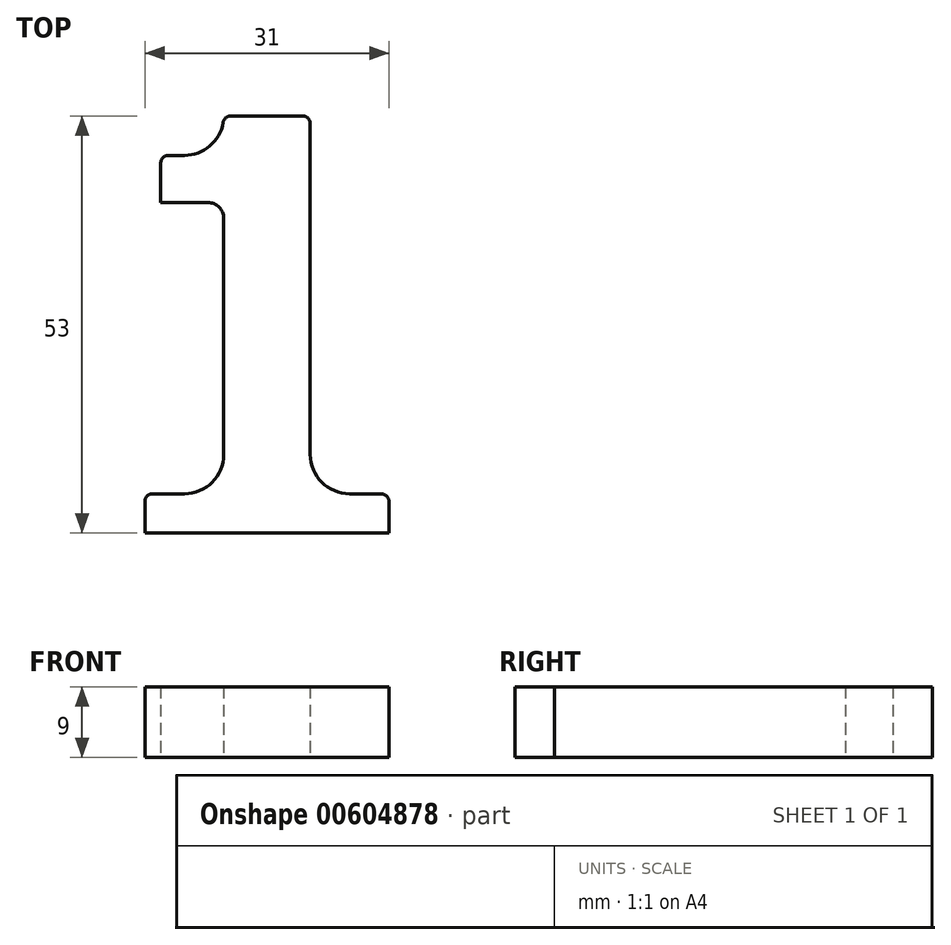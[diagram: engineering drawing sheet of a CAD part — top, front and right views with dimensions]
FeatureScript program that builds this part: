
annotation { "Feature Type Name" : "Feature", "Feature Type Description" : "" }
export const myFeature = defineFeature(function(context is Context, id is Id, definition is map)
    precondition{}
    {
        {
            var Q0;
            Q0=qCreatedBy(makeId("Top.planeOp"),FACE);
            var sketch = newSketch(context, id + "F0", { "sketchPlane" : qUnion([Q0])});
            skLineSegment(sketch, "E0.bottom", {"start": v(5.5, -26.5) * mm, "end": v(-5.5, -26.5) * mm});
            skLineSegment(sketch, "E0.top", {"start": v(5.5, 26.5) * mm, "end": v(-5.5, 26.5) * mm});
            skLineSegment(sketch, "E0.left", {"start": v(5.5, -16.5) * mm, "end": v(5.5, 26.5) * mm});
            skLineSegment(sketch, "E0.right", {"start": v(-5.5, 26.5) * mm, "end": v(-5.5, 26.5) * mm});
            skPoint(sketch, "E0.middle", {"position": v(0, 0) * mm});
            skLineSegment(sketch, "E1.bottom", {"start": v(-5.5, -26.5) * mm, "end": v(-15.5, -26.5) * mm});
            skLineSegment(sketch, "E1.top", {"start": v(-10.5, -21.5) * mm, "end": v(-14.5, -21.5) * mm});
            skLineSegment(sketch, "E1.right", {"start": v(-15.5, -26.5) * mm, "end": v(-15.5, -22.5) * mm});
            skArc(sketch, "E2.filletArc", {"start": v(-10.5, -21.5) * mm, "mid": v(-6.96, -20.04) * mm, "end": v(-5.5, -16.5) * mm});
            skPoint(sketch, "E3.visualSharp", {"position": v(-15.5, -21.5) * mm});
            skArc(sketch, "E3.filletArc", {"start": v(-14.5, -21.5) * mm, "mid": v(-15.2, -21.8) * mm, "end": v(-15.5, -22.5) * mm});
            skLineSegment(sketch, "E4", {"start": v(0, 26.5) * mm, "end": v(0, -26.5) * mm, "construction": true});
            skArc(sketch, "E5.MirrorCS", {"start": v(10.5, -21.5) * mm, "mid": v(6.96, -20.04) * mm, "end": v(5.5, -16.5) * mm});
            skLineSegment(sketch, "E6.MirrorCS", {"start": v(10.5, -21.5) * mm, "end": v(14.5, -21.5) * mm});
            skArc(sketch, "E7.MirrorCS", {"start": v(14.5, -21.5) * mm, "mid": v(15.2, -21.8) * mm, "end": v(15.5, -22.5) * mm});
            skLineSegment(sketch, "E8.MirrorCS", {"start": v(15.5, -26.5) * mm, "end": v(15.5, -22.5) * mm});
            skLineSegment(sketch, "E9.MirrorCS", {"start": v(5.5, -26.5) * mm, "end": v(15.5, -26.5) * mm});
            skLineSegment(sketch, "E10.bottom", {"start": v(-10.5, 21.5) * mm, "end": v(-12.5, 21.5) * mm});
            skLineSegment(sketch, "E10.top", {"start": v(-7.5, 15.5) * mm, "end": v(-13.5, 15.5) * mm});
            skLineSegment(sketch, "E10.right", {"start": v(-13.5, 20.5) * mm, "end": v(-13.5, 15.5) * mm});
            skArc(sketch, "E11.filletArc", {"start": v(-10.5, 21.5) * mm, "mid": v(-6.96, 22.96) * mm, "end": v(-5.5, 26.5) * mm});
            skLineSegment(sketch, "E12", {"start": v(-5.5, 13.5) * mm, "end": v(-5.5, -16.5) * mm});
            skPoint(sketch, "E13.visualSharp", {"position": v(-13.5, 21.5) * mm});
            skArc(sketch, "E13.filletArc", {"start": v(-12.5, 21.5) * mm, "mid": v(-13.2, 21.2) * mm, "end": v(-13.5, 20.5) * mm});
            skPoint(sketch, "E14.visualSharp", {"position": v(-5.5, 15.5) * mm});
            skArc(sketch, "E14.filletArc", {"start": v(-5.5, 13.5) * mm, "mid": v(-6.09, 14.91) * mm, "end": v(-7.5, 15.5) * mm});
            skSolve(sketch);
        }
        {
            var Q0;
            Q0 = qSketchRegion(id + "F0", true);
            extrude(context, id + "F1", {"entities" : qUnion([Q0]), "depth" : 9 * mm, "offsetDistance" : 25 * mm, "symmetric" : true});
        }
        {
            var Q0;
            Q0=makeQuery(id+"F1.opExtrude","SWEPT_EDGE",EDGE,{"disambiguationData":[OSD([sQuery(id+"F0.wireOp",EDGE,"E0.top"),sQuery(id+"F0.wireOp",EDGE,"E0.left")])]});
            var Q1;
            Q1=makeQuery(id+"F1.opExtrude","SWEPT_EDGE",EDGE,{"disambiguationData":[OSD([sQuery(id+"F0.wireOp",EDGE,"E0.top"),sQuery(id+"F0.wireOp",EDGE,"E11.filletArc")])]});
            fillet(context, id + "F2", {"entities" : qUnion([Q0, Q1]), "radius" : 1 * mm, "tangentPropagation" : true, "allowEdgeOverflow" : false});
        }
    });
